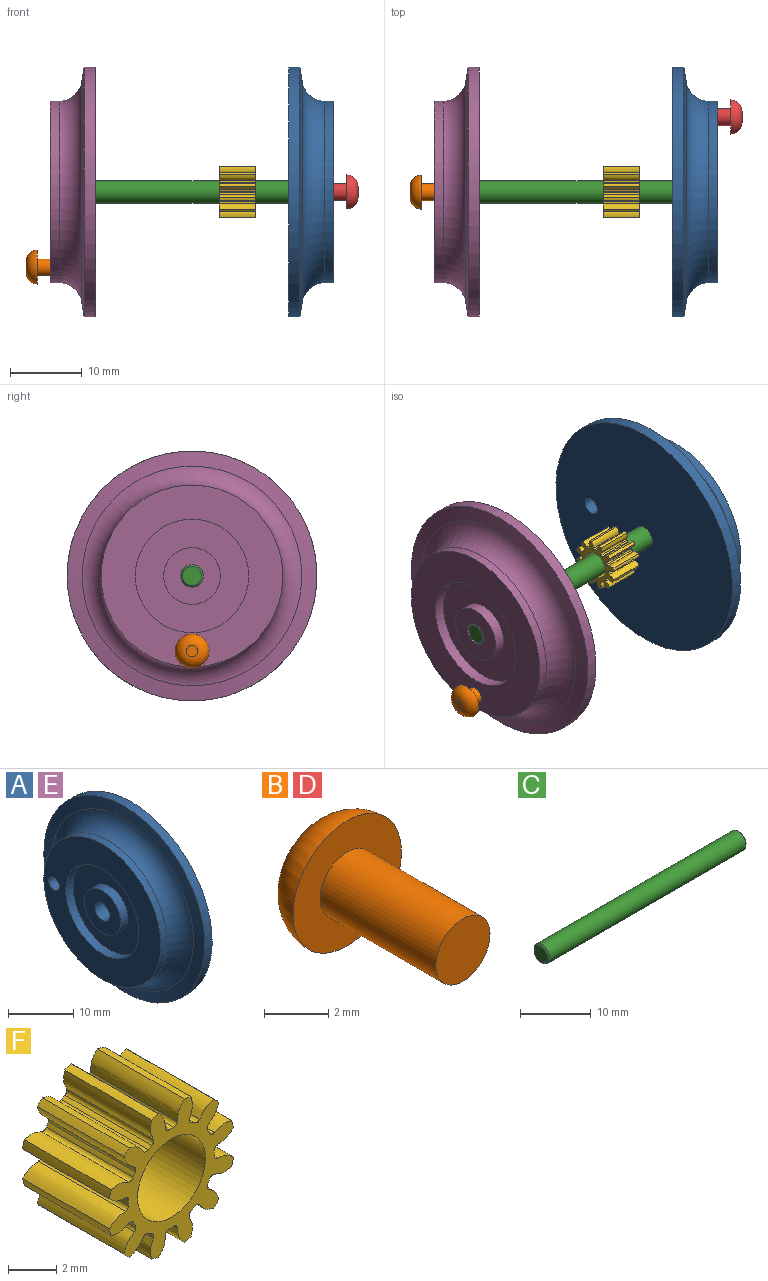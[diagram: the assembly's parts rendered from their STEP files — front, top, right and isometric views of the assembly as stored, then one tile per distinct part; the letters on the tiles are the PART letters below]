
ASSEMBLY  parts=6 mates=5
PART A: 12 faces, bbox 6.4x34.9x34.9 mm
  f0: cylinder r=17.46mm len=34.93mm, axis (-1,0,0), area 174.2mm2, adj f1,f9
  f1: cone r=17.46mm half-angle=80.5deg, axis (1,0,0), area 220.5mm2, adj f0,f2
  f2: torus R=15.88mm, axis (-1,0,0), area 382.7mm2, adj f1,f3
  f3: cylinder r=12.7mm len=25.4mm, axis (-1,0,0), area 102.1mm2, adj f2,f4
  f4: plane 25.4x25.4mm, normal (-1,0,0), area 304.3mm2, adj f3,f5,f11
  f5: cylinder r=7.94mm len=15.88mm, axis (-1,0,0), area 78.5mm2, adj f4,f6
  f6: plane 15.88x15.88mm, normal (-1,0,0), area 148.4mm2, adj f5,f7
  f7: cylinder r=3.97mm len=7.94mm, axis (-1,0,0), area 39.3mm2, adj f6,f8
  f8: plane 7.94x7.94mm, normal (-1,0,0), area 41.6mm2, adj f7,f10
  f9: plane 34.93x34.93mm, normal (1,0,0), area 945.6mm2, adj f0,f10,f11
  f10: cylinder r=1.59mm len=6.35mm, axis (1,0,0), area 63.3mm2, adj f8,f9
  f11: cylinder r=1.19mm len=6.35mm, axis (-1,0,0), area 47.5mm2, adj f4,f9
PART B: 5 faces, bbox 4.8x6.7x4.8 mm
  f0: cylinder r=1.19mm len=5.08mm, axis (0,1,0), area 38mm2, adj f1,f3
  f1: plane 2.38x2.38mm, normal (0,-1,0), area 4.5mm2, adj f0
  f2: plane 1.59x1.59mm, normal (0,1,0), area 2mm2, adj f4
  f3: plane 4.76x4.76mm, normal (0,-1,0), area 13.4mm2, adj f0,f4
  f4: torus R=0.79mm, axis (0,-1,0), area 28.3mm2, adj f2,f3
PART C: 5 faces, bbox 39.7x3.2x3.2 mm
  f0: cylinder r=1.59mm len=39.18mm, axis (-1,0,0), area 390.8mm2, adj f3,f4
  f1: plane 2.67x2.67mm, normal (1,0,0), area 5.6mm2, adj f4
  f2: plane 2.67x2.67mm, normal (-1,0,0), area 5.6mm2, adj f3
  f3: cone r=1.59mm half-angle=45deg, axis (1,0,0), area 3.3mm2, adj f0,f2
  f4: cone r=1.33mm half-angle=45deg, axis (-1,0,0), area 3.3mm2, adj f0,f1
PART D: same geometry as B
PART E: same geometry as A
PART F: 75 faces, bbox 7.3x5.1x7.3 mm
  f0: extruded ~5.08x0.93mm, area 5.4mm2, adj f47,f48,f49,f50
  f1: cylinder r=2.51mm len=5.08mm, axis (0,1,0), area 1.2mm2, adj f48,f49,f50,f51
  f2: extruded ~5.08x0.93mm, area 5.4mm2, adj f3,f48,f49,f51
  f3: cylinder r=3.7mm len=5.08mm, axis (0,1,0), area 2.1mm2, adj f2,f4,f48,f49
  f4: extruded ~5.08x1.01mm, area 5.4mm2, adj f3,f48,f49,f52
  f5: cylinder r=2.51mm len=5.08mm, axis (0,1,0), area 1.2mm2, adj f48,f49,f52,f53
  f6: extruded ~5.08x0.82mm, area 5.4mm2, adj f7,f48,f49,f53
  f7: cylinder r=3.7mm len=5.08mm, axis (0,1,0), area 2.1mm2, adj f6,f8,f48,f49
  f8: extruded ~5.08x0.82mm, area 5.4mm2, adj f7,f48,f49,f54
  f9: cylinder r=2.51mm len=5.08mm, axis (0,1,0), area 1.2mm2, adj f48,f49,f54,f55
  f10: extruded ~5.08x1.01mm, area 5.4mm2, adj f11,f48,f49,f55
  f11: cylinder r=3.7mm len=5.08mm, axis (0,1,0), area 2.1mm2, adj f10,f12,f48,f49
  f12: extruded ~5.08x0.93mm, area 5.4mm2, adj f11,f48,f49,f56
  f13: cylinder r=2.51mm len=5.08mm, axis (0,1,0), area 1.2mm2, adj f48,f49,f56,f57
  f14: extruded ~5.08x0.93mm, area 5.4mm2, adj f15,f48,f49,f57
  f15: cylinder r=3.7mm len=5.08mm, axis (0,1,0), area 2.1mm2, adj f14,f16,f48,f49
  f16: extruded ~5.08x1.01mm, area 5.4mm2, adj f15,f48,f49,f58
  f17: cylinder r=2.51mm len=5.08mm, axis (0,1,0), area 1.2mm2, adj f48,f49,f58,f59
  f18: extruded ~5.08x0.82mm, area 5.4mm2, adj f19,f48,f49,f59
  f19: cylinder r=3.7mm len=5.08mm, axis (0,1,0), area 2.1mm2, adj f18,f20,f48,f49
  f20: extruded ~5.08x0.82mm, area 5.4mm2, adj f19,f48,f49,f60
  f21: cylinder r=2.51mm len=5.08mm, axis (0,1,0), area 1.2mm2, adj f48,f49,f60,f61
  f22: extruded ~5.08x1.01mm, area 5.4mm2, adj f23,f48,f49,f61
  f23: cylinder r=3.7mm len=5.08mm, axis (0,1,0), area 2.1mm2, adj f22,f24,f48,f49
  f24: extruded ~5.08x0.93mm, area 5.4mm2, adj f23,f48,f49,f62
  f25: cylinder r=2.51mm len=5.08mm, axis (0,1,0), area 1.2mm2, adj f48,f49,f62,f63
  f26: extruded ~5.08x0.93mm, area 5.4mm2, adj f27,f48,f49,f63
  f27: cylinder r=3.7mm len=5.08mm, axis (0,1,0), area 2.1mm2, adj f26,f28,f48,f49
  f28: extruded ~5.08x1.01mm, area 5.4mm2, adj f27,f48,f49,f64
  f29: cylinder r=2.51mm len=5.08mm, axis (0,1,0), area 1.2mm2, adj f48,f49,f64,f65
  f30: extruded ~5.08x0.82mm, area 5.4mm2, adj f31,f48,f49,f65
  f31: cylinder r=3.7mm len=5.08mm, axis (0,1,0), area 2.1mm2, adj f30,f32,f48,f49
  f32: extruded ~5.08x0.82mm, area 5.4mm2, adj f31,f48,f49,f66
  f33: cylinder r=2.51mm len=5.08mm, axis (0,1,0), area 1.2mm2, adj f48,f49,f66,f67
  f34: extruded ~5.08x1.01mm, area 5.4mm2, adj f35,f48,f49,f67
  f35: cylinder r=3.7mm len=5.08mm, axis (0,1,0), area 2.1mm2, adj f34,f36,f48,f49
  f36: extruded ~5.08x0.93mm, area 5.4mm2, adj f35,f48,f49,f68
  f37: cylinder r=2.51mm len=5.08mm, axis (0,1,0), area 1.2mm2, adj f48,f49,f68,f69
  f38: extruded ~5.08x0.93mm, area 5.4mm2, adj f39,f48,f49,f69
  f39: cylinder r=3.7mm len=5.08mm, axis (0,1,0), area 2.1mm2, adj f38,f40,f48,f49
  f40: extruded ~5.08x1.01mm, area 5.4mm2, adj f39,f48,f49,f70
  f41: cylinder r=2.51mm len=5.08mm, axis (0,1,0), area 1.2mm2, adj f48,f49,f70,f71
  f42: extruded ~5.08x0.82mm, area 5.4mm2, adj f43,f48,f49,f71
  f43: cylinder r=3.7mm len=5.08mm, axis (0,1,0), area 2.1mm2, adj f42,f44,f48,f49
  f44: extruded ~5.08x0.82mm, area 5.4mm2, adj f43,f48,f49,f72
  f45: cylinder r=2.51mm len=5.08mm, axis (0,1,0), area 1.2mm2, adj f48,f49,f72,f73
  f46: extruded ~5.08x1.01mm, area 5.4mm2, adj f47,f48,f49,f73
  f47: cylinder r=3.7mm len=5.08mm, axis (0,1,0), area 2.1mm2, adj f0,f46,f48,f49
  f48: plane 7.28x7.28mm, normal (0,-1,0), area 18.1mm2, adj f0,f1,f2,f3,f4,f5,f6,f7
  f49: plane 7.28x7.28mm, normal (0,1,0), area 18.1mm2, adj f0,f1,f2,f3,f4,f5,f6,f7
  f50: cylinder r=0.21mm len=5.08mm, axis (0,1,0), area 1.6mm2, adj f0,f1,f48,f49
  f51: cylinder r=0.21mm len=5.08mm, axis (0,1,0), area 1.6mm2, adj f1,f2,f48,f49
  f52: cylinder r=0.21mm len=5.08mm, axis (0,1,0), area 1.6mm2, adj f4,f5,f48,f49
  f53: cylinder r=0.21mm len=5.08mm, axis (0,1,0), area 1.6mm2, adj f5,f6,f48,f49
  f54: cylinder r=0.21mm len=5.08mm, axis (0,1,0), area 1.6mm2, adj f8,f9,f48,f49
  f55: cylinder r=0.21mm len=5.08mm, axis (0,1,0), area 1.6mm2, adj f9,f10,f48,f49
  f56: cylinder r=0.21mm len=5.08mm, axis (0,1,0), area 1.6mm2, adj f12,f13,f48,f49
  f57: cylinder r=0.21mm len=5.08mm, axis (0,1,0), area 1.6mm2, adj f13,f14,f48,f49
  f58: cylinder r=0.21mm len=5.08mm, axis (0,1,0), area 1.6mm2, adj f16,f17,f48,f49
  f59: cylinder r=0.21mm len=5.08mm, axis (0,1,0), area 1.6mm2, adj f17,f18,f48,f49
  f60: cylinder r=0.21mm len=5.08mm, axis (0,1,0), area 1.6mm2, adj f20,f21,f48,f49
  f61: cylinder r=0.21mm len=5.08mm, axis (0,1,0), area 1.6mm2, adj f21,f22,f48,f49
  f62: cylinder r=0.21mm len=5.08mm, axis (0,1,0), area 1.6mm2, adj f24,f25,f48,f49
  f63: cylinder r=0.21mm len=5.08mm, axis (0,1,0), area 1.6mm2, adj f25,f26,f48,f49
  f64: cylinder r=0.21mm len=5.08mm, axis (0,1,0), area 1.6mm2, adj f28,f29,f48,f49
  f65: cylinder r=0.21mm len=5.08mm, axis (0,1,0), area 1.6mm2, adj f29,f30,f48,f49
  f66: cylinder r=0.21mm len=5.08mm, axis (0,1,0), area 1.6mm2, adj f32,f33,f48,f49
  f67: cylinder r=0.21mm len=5.08mm, axis (0,1,0), area 1.6mm2, adj f33,f34,f48,f49
  f68: cylinder r=0.21mm len=5.08mm, axis (0,1,0), area 1.6mm2, adj f36,f37,f48,f49
  f69: cylinder r=0.21mm len=5.08mm, axis (0,1,0), area 1.6mm2, adj f37,f38,f48,f49
  f70: cylinder r=0.21mm len=5.08mm, axis (0,1,0), area 1.6mm2, adj f40,f41,f48,f49
  f71: cylinder r=0.21mm len=5.08mm, axis (0,1,0), area 1.6mm2, adj f41,f42,f48,f49
  f72: cylinder r=0.21mm len=5.08mm, axis (0,1,0), area 1.6mm2, adj f44,f45,f48,f49
  f73: cylinder r=0.21mm len=5.08mm, axis (0,1,0), area 1.6mm2, adj f45,f46,f48,f49
  f74: cylinder r=1.98mm len=5.08mm, axis (0,1,0), area 63.3mm2, adj f48,f49
PLACE A rot(axis=(0,1,0),180deg) t=(22.52,0.23,-1.98)mm
PLACE B rot(axis=(0,0,1),90deg) t=(-18.94,0.23,-12.47)mm
PLACE C t=(-17.16,0.23,-1.98)mm
PLACE D rot(axis=(0.58,0.58,-0.58),120deg) t=(24.3,10.72,-1.98)mm
PLACE E rot(axis=(-1,0,0),90deg) t=(-17.16,0.23,-1.98)mm
PLACE F rot(axis=(0.58,-0.58,0.58),120deg) t=(6.47,0.23,-1.98)mm
MATE fastened B.f0 <-> E.f11  axis (-1,0,0) through (-18.94,0.23,-12.47)mm
MATE fastened A.f10 <-> C.f0  axis (1,0,0) through (22.52,0.23,-1.98)mm
MATE slider F.f74 <-> C.f0  axis (-1,0,0) through (11.55,0.23,-1.98)mm
MATE fastened D.f0 <-> A.f11  axis (-1,0,0) through (24.3,10.72,-1.98)mm
MATE fastened E.f10 <-> C.f0  axis (1,0,0) through (-17.16,0.23,-1.98)mm
